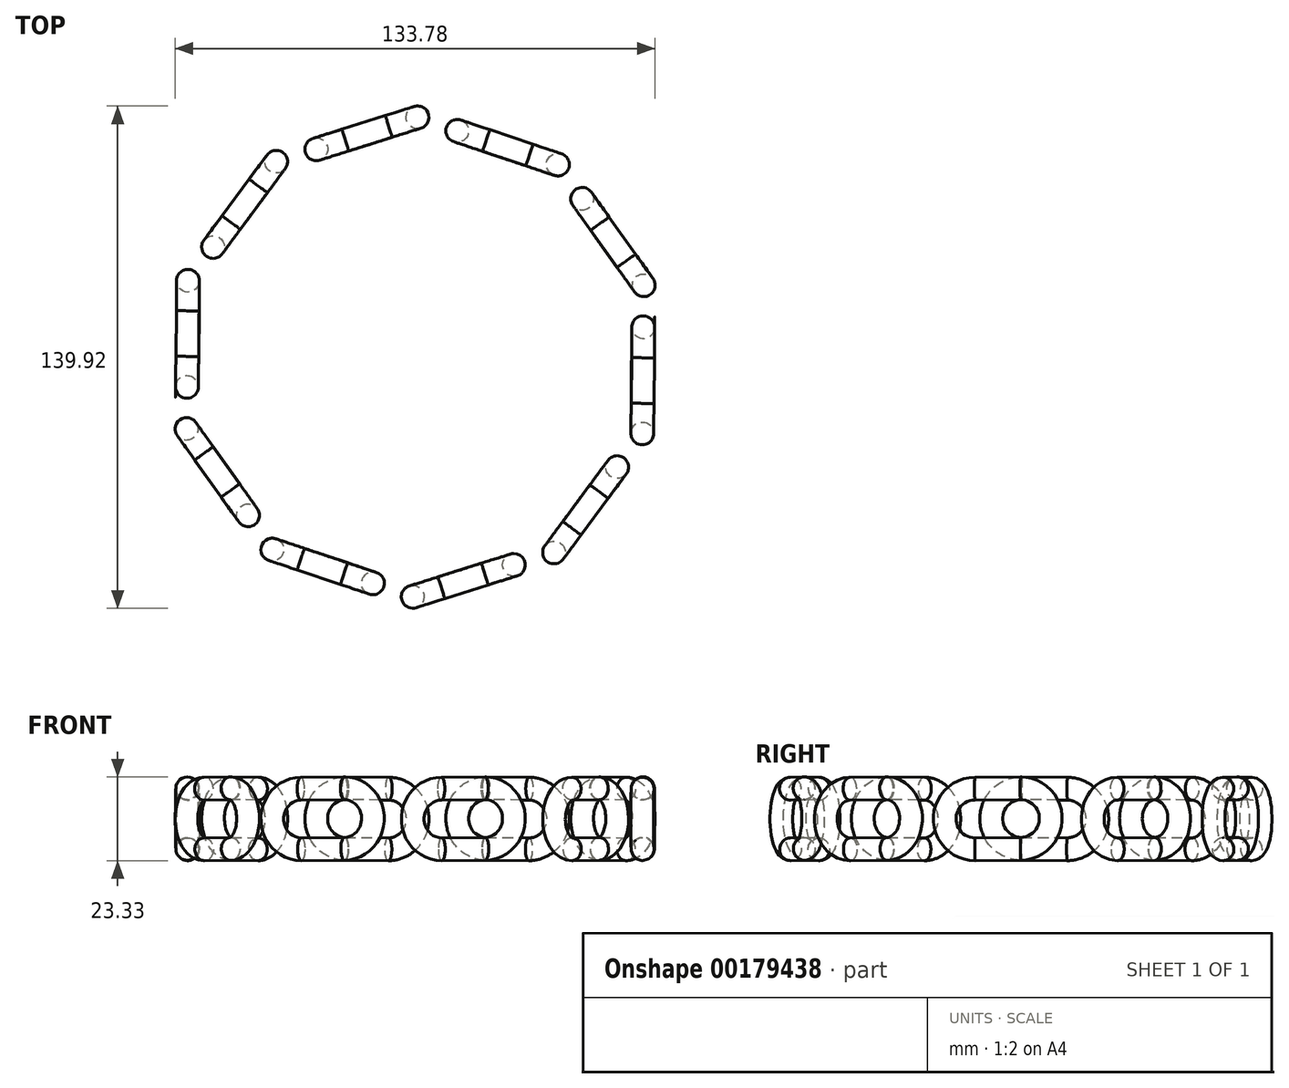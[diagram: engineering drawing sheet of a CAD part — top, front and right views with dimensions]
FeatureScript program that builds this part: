
annotation { "Feature Type Name" : "Feature", "Feature Type Description" : "" }
export const myFeature = defineFeature(function(context is Context, id is Id, definition is map)
    precondition{}
    {
        {
            var Q0;
            Q0=qCreatedBy(makeId("Top.planeOp"),FACE);
            var sketch = newSketch(context, id + "F0", { "sketchPlane" : qUnion([Q0])});
            skLineSegment(sketch, "E0.bottom", {"start": v(-14.78, -12.76) * mm, "end": v(-2.08, -12.76) * mm, "construction": true});
            skLineSegment(sketch, "E0.top", {"start": v(-14.78, -0.06) * mm, "end": v(-2.08, -0.06) * mm, "construction": true});
            skLineSegment(sketch, "E0.left", {"start": v(-14.78, -12.76) * mm, "end": v(-14.78, -0.06) * mm});
            skLineSegment(sketch, "E0.right", {"start": v(-2.08, -12.76) * mm, "end": v(-2.08, -0.06) * mm});
            skArc(sketch, "E1", {"start": v(-14.78, -0.06) * mm, "mid": v(-8.43, 6.3) * mm, "end": v(-2.08, -0.06) * mm});
            skArc(sketch, "E2", {"start": v(-14.78, -12.76) * mm, "mid": v(-8.43, -19.1) * mm, "end": v(-2.08, -12.76) * mm});
            skSolve(sketch);
        }
        {
            var Q0;
            Q0=qCreatedBy(makeId("Front.planeOp"),FACE);
            var sketch = newSketch(context, id + "F1", { "sketchPlane" : qUnion([Q0])});
            skCircle(sketch, "E3", {"center": v(0, 0) * mm, "radius": 3.17 * mm});
            skSolve(sketch);
        }
        {
            var Q0;
            Q0 = qSketchRegion(id + "F1", true);
            var Q1;
            Q1 = qConstructionFilter(qBodyType(qCreatedBy(id + "F0" ,EDGE), BodyType.WIRE), ConstructionObject.NO);
            sweep(context, id + "F2", {"profiles" : qUnion([Q0]), "path" : qUnion([Q1])});
        }
        {
            var Q0;
            Q0=qCreatedBy(makeId("Top.planeOp"),FACE);
            var sketch = newSketch(context, id + "F3", { "sketchPlane" : qUnion([Q0])});
            skCircle(sketch, "E4", {"center": v(0, 0) * mm, "radius": 63.5 * mm});
            skSolve(sketch);
        }
        {
            var Q0;
            Q0=makeQuery(id+"F2.opSweep","SWEPT_BODY",BODY,{"disambiguationData":[OSD([sQuery(id+"F0.wireOp",EDGE,"E2"),sQuery(id+"F1.wireOp",EDGE,"E3")])]});
            var Q1;
            Q1=makeQuery(id+"F2.opSweep","CAP_EDGE",EDGE,{"disambiguationData":[OSD([sQuery(id+"F0.wireOp",VERTEX,"E1.end"),sQuery(id+"F1.wireOp",EDGE,"E3")])],"isStart":true});
            transform(context, id + "F4", {"entities" : qUnion([Q0]), "transformType" : TransformType.ROTATION, "transformAxis" : qUnion([Q1]), "angle" : 90 * degree, "oppositeDirection" : true, "makeCopy" : false});
        }
        {
            var Q0;
            Q0=makeQuery(id+"F2.opSweep","SWEPT_BODY",BODY,{"disambiguationData":[OSD([sQuery(id+"F0.wireOp",EDGE,"E2"),sQuery(id+"F1.wireOp",EDGE,"E3")])]});
            var Q1;
            Q1=sQuery(id+"F3.wireOp",EDGE,"E4");
            var Q2;
            Q2=qCreatedBy(makeId("Right.planeOp"),FACE);
            transform(context, id + "F5", {"entities" : qUnion([Q0]), "transformType" : TransformType.TRANSLATION_DISTANCE, "transformDirection" : qUnion([Q2]), "distance" : 63.5 * mm, "makeCopy" : false});
        }
        {
            var Q0;
            Q0=makeQuery(id+"F2.opSweep","SWEPT_BODY",BODY,{"disambiguationData":[OSD([sQuery(id+"F0.wireOp",EDGE,"E2"),sQuery(id+"F1.wireOp",EDGE,"E3")])]});
            var Q1;
            Q1=sQuery(id+"F3.wireOp",EDGE,"E4");
            circularPattern(context, id + "F6", {"entities" : qUnion([Q0]), "axis" : qUnion([Q1]), "angle" : 360 * degree, "instanceCount" : 10, "equalSpace" : true});
        }
    });
